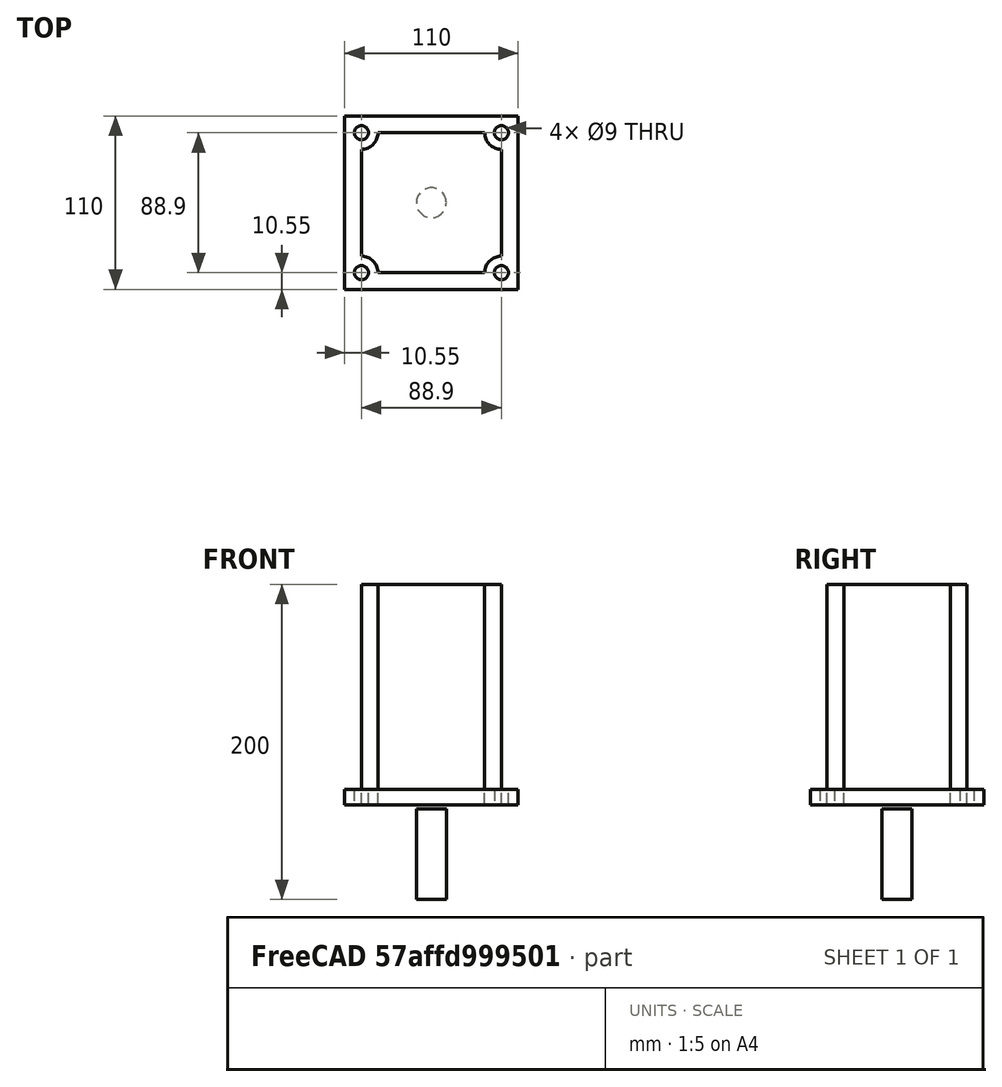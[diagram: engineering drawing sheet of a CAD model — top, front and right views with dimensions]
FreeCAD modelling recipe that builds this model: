
FCSTD DOCUMENT  (FreeCAD 0.20R29177 +426 (Git))
Label: nema42-20nm
License: All rights reserved
LicenseURL: http://en.wikipedia.org/wiki/All_rights_reserved
objects: Sketcher::SketchObject×2, Part::Extrusion×2, PartDesign::ShapeBinder×2, PartDesign::Body×1, Part::Cylinder×1
note: 8 computed .brp shape members not serialized (recipe doc carries the construction recipe); baked Part::Feature solids carry a one-line shape summary decoded from their .brp

FEATURE [Sketcher::SketchObject] Sketch
  FullyConstrained = true
  MapMode = 5
  Support = -> [XY_Plane]
  sketch-geometry (14):
    g0: LineSegment StartX=-44.45 StartY=-44.45 StartZ=0 EndX=-44.45 EndY=44.45 EndZ=0
    g1: LineSegment StartX=-44.45 StartY=44.45 StartZ=0 EndX=44.45 EndY=44.45 EndZ=0
    g2: LineSegment StartX=44.45 StartY=44.45 StartZ=0 EndX=44.45 EndY=-44.45 EndZ=0
    g3: LineSegment StartX=44.45 StartY=-44.45 StartZ=0 EndX=-44.45 EndY=-44.45 EndZ=0
    g4: GeomPoint X=0 Y=0 Z=0
    g5: LineSegment StartX=-55 StartY=-55 StartZ=0 EndX=-55 EndY=55 EndZ=0
    g6: LineSegment StartX=-55 StartY=55 StartZ=0 EndX=55 EndY=55 EndZ=0
    g7: LineSegment StartX=55 StartY=55 StartZ=0 EndX=55 EndY=-55 EndZ=0
    g8: LineSegment StartX=55 StartY=-55 StartZ=0 EndX=-55 EndY=-55 EndZ=0
    g9: GeomPoint X=0 Y=0 Z=0
    g10: Circle CenterX=-44.45 CenterY=44.45 CenterZ=0 NormalX=0 NormalY=0 NormalZ=1 AngleXU=0 Radius=4.5
    g11: Circle CenterX=44.45 CenterY=44.45 CenterZ=0 NormalX=0 NormalY=0 NormalZ=1 AngleXU=0 Radius=4.5
    g12: Circle CenterX=44.45 CenterY=-44.45 CenterZ=0 NormalX=0 NormalY=0 NormalZ=1 AngleXU=0 Radius=4.5
    g13: Circle CenterX=-44.45 CenterY=-44.45 CenterZ=0 NormalX=0 NormalY=0 NormalZ=1 AngleXU=0 Radius=4.5
  constraints (32):
    c: Coincident(g0,g1)
    c: Coincident(g1,g2)
    c: Coincident(g2,g3)
    c: Coincident(g3,g0)
    c: Horizontal(g1)
    c: Horizontal(g3)
    c: Vertical(g0)
    c: Vertical(g2)
    c: Symmetric(g1,g0,g4)
    c: Coincident(g4,g-1)
    c: Equal(g1,g0)
    c: DistanceX(g3,g3) = 88.9
    c: Coincident(g5,g6)
    c: Coincident(g6,g7)
    c: Coincident(g7,g8)
    c: Coincident(g8,g5)
    c: Horizontal(g6)
    c: Horizontal(g8)
    c: Vertical(g5)
    c: Vertical(g7)
    c: Symmetric(g6,g5,g9)
    c: Coincident(g9,g4)
    c: DistanceX(g8,g8) = 110
    c: Equal(g5,g8)
    c: Coincident(g10,g0)
    c: Coincident(g11,g1)
    c: Coincident(g12,g2)
    c: Coincident(g13,g0)
    c: Equal(g10,g11)
    c: Equal(g10,g13)
    c: Equal(g12,g11)
    c: Diameter(g10) = 9
FEATURE [Part::Extrusion] Extrude
  Base = -> Sketch
  Dir = (0,0,1)
  DirMode = 2
  FaceMakerClass = Part::FaceMakerBullseye
  LengthFwd = 10
  LengthRev = 0
  Solid = true
  Symmetric = false
FEATURE [PartDesign::ShapeBinder] ShapeBinder
  TraceSupport = false
FEATURE [PartDesign::ShapeBinder] CopyExtrude
  Placement = pos=(0,0,150) rot=(0,0,1;0rad)
  TraceSupport = false
FEATURE [Sketcher::SketchObject] Sketch001
  FullyConstrained = false
  MapMode = 5
  Placement = pos=(0,0,150) rot=(0,0,1;0rad)
  Support = -> [CopyExtrude]
  sketch-geometry (9):
    g0: GeomPoint X=0 Y=0 Z=0
    g1: ArcOfCircle CenterX=44.45 CenterY=-44.45 CenterZ=0 NormalX=0 NormalY=0 NormalZ=1 AngleXU=0 Radius=10.55 StartAngle=1.5708 EndAngle=3.14159
    g2: ArcOfCircle CenterX=44.45 CenterY=44.45 CenterZ=0 NormalX=0 NormalY=0 NormalZ=1 AngleXU=0 Radius=10.55 StartAngle=3.14159 EndAngle=4.71239
    g3: ArcOfCircle CenterX=-44.45 CenterY=44.45 CenterZ=0 NormalX=0 NormalY=0 NormalZ=1 AngleXU=0 Radius=10.55 StartAngle=4.71239 EndAngle=6.28319
    g4: LineSegment StartX=-33.9 StartY=44.45 StartZ=0 EndX=33.9 EndY=44.45 EndZ=0
    g5: LineSegment StartX=44.45 StartY=33.9 StartZ=0 EndX=44.45 EndY=-33.9 EndZ=0
    g6: LineSegment StartX=33.9 StartY=-44.45 StartZ=0 EndX=-33.9 EndY=-44.45 EndZ=0
    g7: LineSegment StartX=-44.45 StartY=-33.9 StartZ=0 EndX=-44.45 EndY=33.9 EndZ=0
    g8: ArcOfCircle CenterX=-44.45 CenterY=-44.45 CenterZ=0 NormalX=0 NormalY=0 NormalZ=1 AngleXU=0 Radius=10.55 StartAngle=0 EndAngle=1.5708
  constraints (9):
    c: Coincident(g0,g-1)
    c: Coincident(g3,g7)
    c: Coincident(g3,g4)
    c: Coincident(g4,g2)
    c: Coincident(g2,g5)
    c: Coincident(g5,g1)
    c: Coincident(g1,g6)
    c: Coincident(g7,g8)
    c: Coincident(g8,g6)
FEATURE [PartDesign::Body] Body
  Group = -> [Sketch,ShapeBinder,CopyExtrude,Sketch001]
  Origin = -> Origin
FEATURE [Part::Extrusion] Extrude002
  Dir = (0,0,1)
  DirMode = 2
  FaceMakerClass = Part::FaceMakerBullseye
  LengthFwd = 140
  LengthRev = 0
  Solid = true
  Symmetric = false
FEATURE [Part::Cylinder] Cylinder
  Angle = 360
  AttacherType = Attacher::AttachEngine3D
  FirstAngle = 0
  Height = 57.5
  Placement = pos=(0,0,-60) rot=(0,0,1;0rad)
  Radius = 9.5
  SecondAngle = 0
